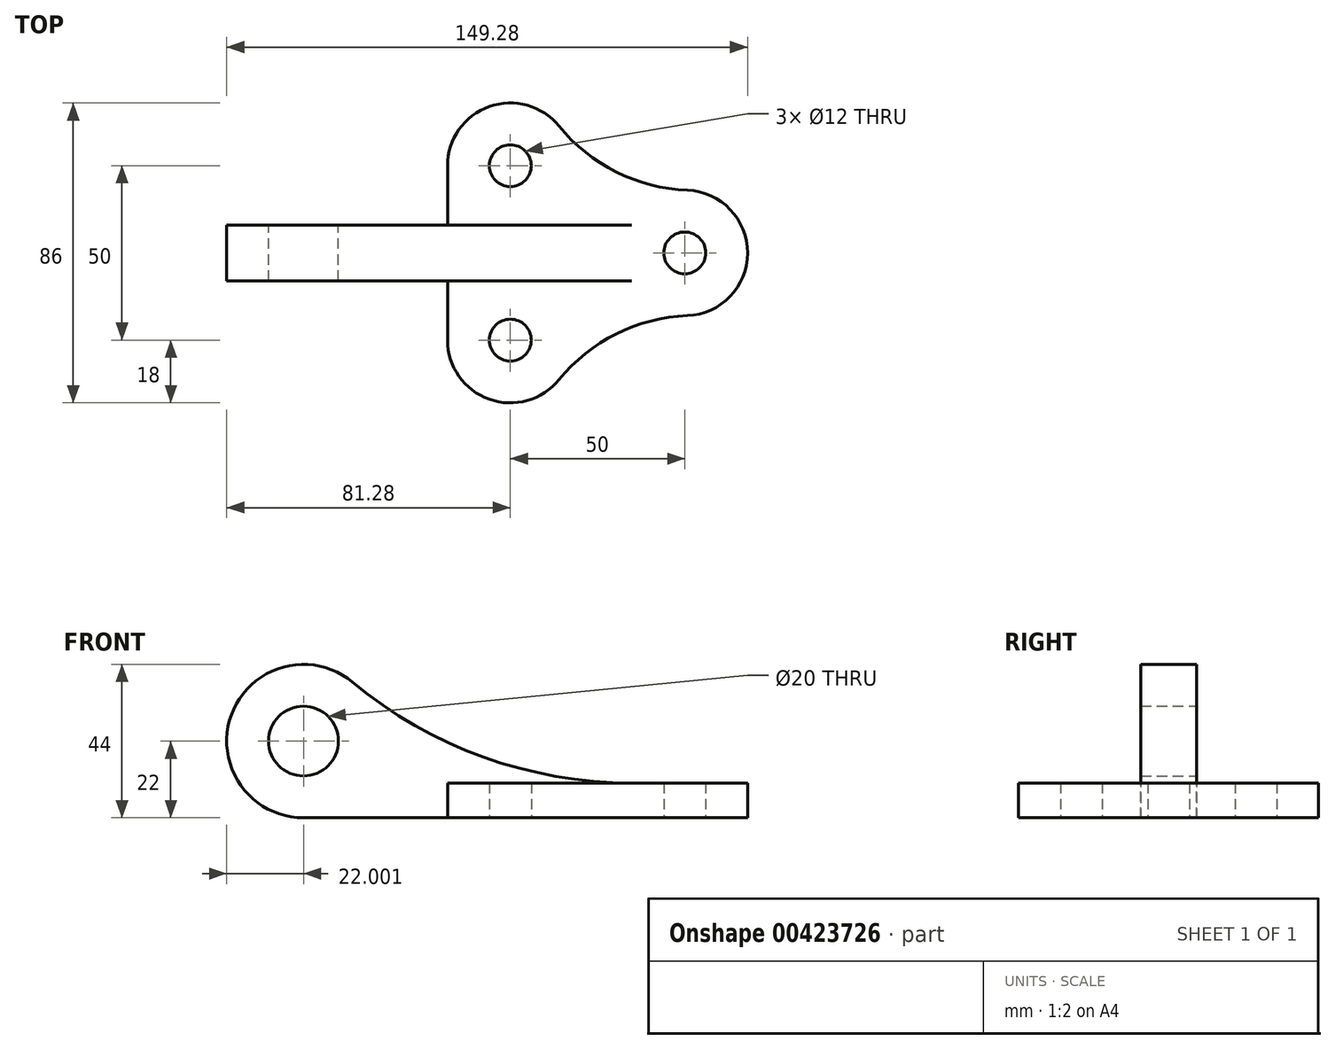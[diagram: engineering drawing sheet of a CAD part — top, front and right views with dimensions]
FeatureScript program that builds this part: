
annotation { "Feature Type Name" : "Feature", "Feature Type Description" : "" }
export const myFeature = defineFeature(function(context is Context, id is Id, definition is map)
    precondition{}
    {
        {
            var Q0;
            Q0=qCreatedBy(makeId("Top.planeOp"),FACE);
            var sketch = newSketch(context, id + "F0", { "sketchPlane" : qUnion([Q0])});
            skCircle(sketch, "E0", {"center": v(0, 0) * mm, "radius": 6 * mm});
            skCircle(sketch, "E1", {"center": v(-50, 25) * mm, "radius": 6 * mm});
            skCircle(sketch, "E2", {"center": v(-50, -25) * mm, "radius": 6 * mm});
            skArc(sketch, "E3", {"start": v(0.72, -17.99) * mm, "mid": v(18, 0) * mm, "end": v(0.72, 17.99) * mm});
            skArc(sketch, "E4", {"start": v(-36.04, 36.37) * mm, "mid": v(-56.03, 41.96) * mm, "end": v(-68, 25) * mm});
            skArc(sketch, "E5", {"start": v(-68, -25) * mm, "mid": v(-56.03, -41.96) * mm, "end": v(-36.04, -36.37) * mm});
            skLineSegment(sketch, "E6", {"start": v(-68, -25) * mm, "end": v(-68, 25) * mm});
            skArc(sketch, "E7", {"start": v(0.72, -17.99) * mm, "mid": v(-19.64, -23.22) * mm, "end": v(-36.04, -36.37) * mm});
            skArc(sketch, "E8.MirrorCS", {"start": v(0.72, 17.99) * mm, "mid": v(-19.64, 23.22) * mm, "end": v(-36.04, 36.37) * mm});
            skSolve(sketch);
        }
        {
            var Q0;
            Q0=makeQuery(id+"F0.imprint","IMPRINT",FACE,{"disambiguationData":[TD([[makeQuery(id+"F0.imprint","IMPRINT",EDGE,{"derivedFrom":sQuery(id+"F0.wireOp",EDGE,"E0")}),-1.0]])]});
            extrude(context, id + "F1", {"entities" : qUnion([Q0]), "depth" : 10 * mm});
        }
        {
            var Q0;
            Q0=qCreatedBy(makeId("Front.planeOp"),FACE);
            var sketch = newSketch(context, id + "F2", { "sketchPlane" : qUnion([Q0])});
            skLineSegment(sketch, "E9.0", {"start": v(0.72, 10) * mm, "end": v(-15.26, 10) * mm});
            skLineSegment(sketch, "E10.0", {"start": v(0.72, 10) * mm, "end": v(18, 10) * mm});
            skLineSegment(sketch, "E11.0", {"start": v(0.72, 10) * mm, "end": v(0.72, 0) * mm});
            skLineSegment(sketch, "E12", {"start": v(0.72, 0) * mm, "end": v(-109.28, 0) * mm});
            skArc(sketch, "E13", {"start": v(-95.2, 38.91) * mm, "mid": v(-129.97, 29.48) * mm, "end": v(-109.28, 0) * mm});
            skCircle(sketch, "E14", {"center": v(-109.28, 22) * mm, "radius": 10 * mm});
            skArc(sketch, "E15", {"start": v(-95.2, 38.91) * mm, "mid": v(-57.77, 17.45) * mm, "end": v(-15.26, 10) * mm});
            skLineSegment(sketch, "E16", {"start": v(-15.26, 10) * mm, "end": v(-15.26, 0) * mm});
            skPoint(sketch, "E17.0.start.orphan", {"position": v(-68, 10) * mm});
            skPoint(sketch, "E18.orphan", {"position": v(-36.04, 10) * mm});
            skSolve(sketch);
        }
        {
            var Q0;
            {var subQ0=sQuery(id+"F2.wireOp",EDGE,"E13");Q0=makeQuery(id+"F2.imprint","IMPRINT",FACE,{"disambiguationData":[TD([[makeQuery(id+"F2.imprint","IMPRINT",EDGE,{"derivedFrom":subQ0}),1.0]])]});}
            extrude(context, id + "F3", {"entities" : qUnion([Q0]), "operationType" : NewBodyOperationType.ADD, "depth" : 8 * mm, "hasSecondDirection" : true, "secondDirectionOppositeDirection" : true, "secondDirectionDepth" : 8 * mm});
        }
    });
